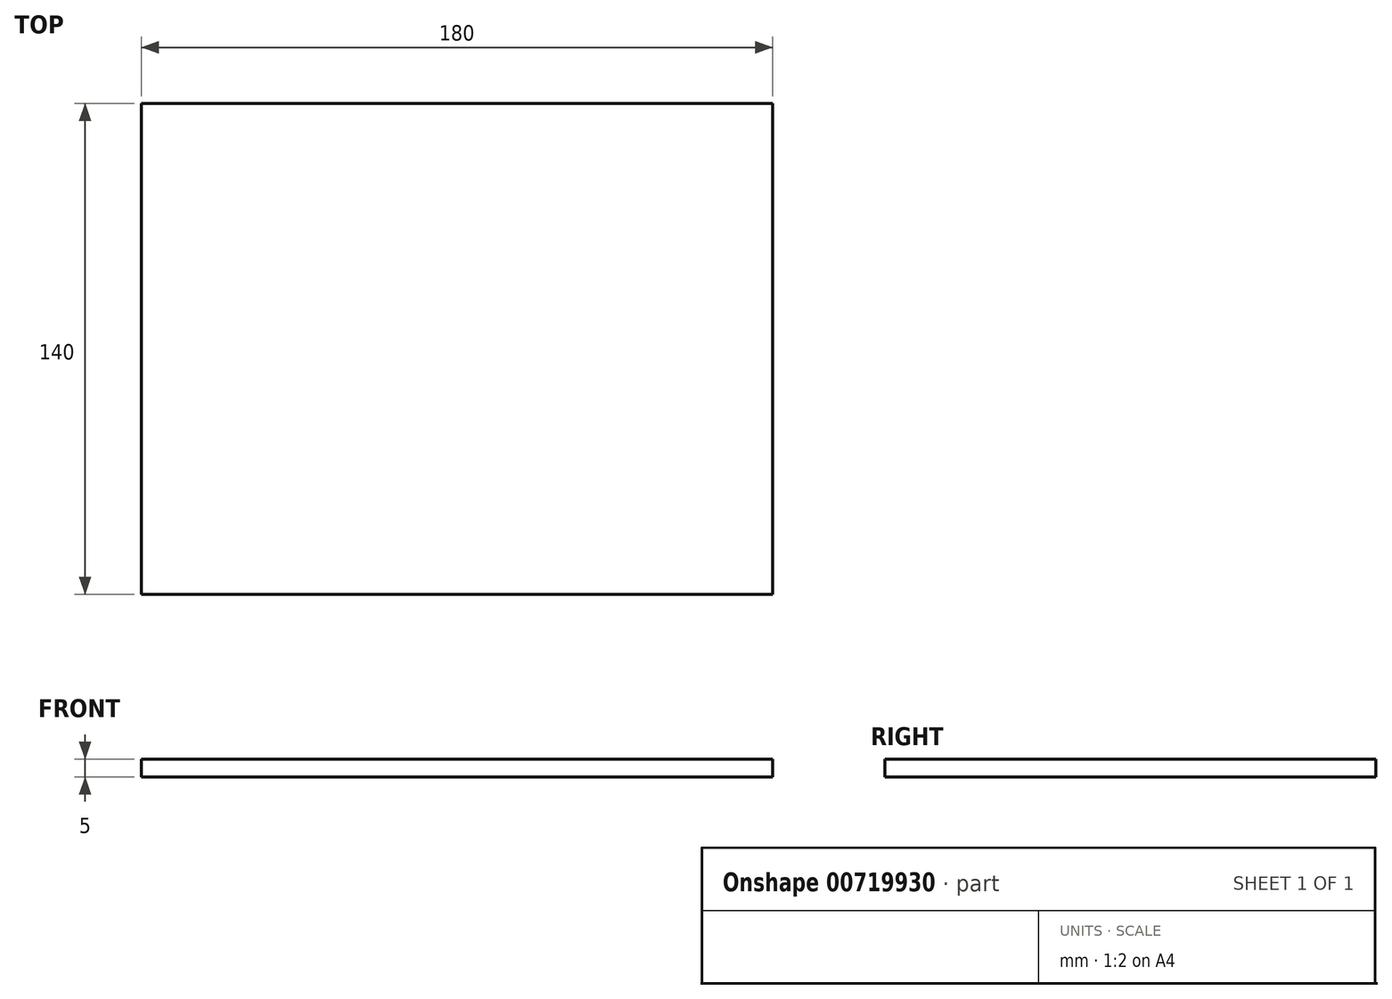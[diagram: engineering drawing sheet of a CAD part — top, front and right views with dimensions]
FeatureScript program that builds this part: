
annotation { "Feature Type Name" : "Feature", "Feature Type Description" : "" }
export const myFeature = defineFeature(function(context is Context, id is Id, definition is map)
    precondition{}
    {
        {
            var Q0;
            Q0=qCreatedBy(makeId("Top.planeOp"),FACE);
            var sketch = newSketch(context, id + "F0", { "sketchPlane" : qUnion([Q0])});
            skLineSegment(sketch, "E0.bottom", {"start": v(-180, 140) * mm, "end": v(0, 140) * mm});
            skLineSegment(sketch, "E0.top", {"start": v(-180, 0) * mm, "end": v(0, 0) * mm});
            skLineSegment(sketch, "E0.left", {"start": v(-180, 140) * mm, "end": v(-180, 0) * mm});
            skLineSegment(sketch, "E0.right", {"start": v(0, 140) * mm, "end": v(0, 0) * mm});
            skSolve(sketch);
        }
        {
            var Q0;
            Q0 = qSketchRegion(id + "F0", true);
            extrude(context, id + "F1", {"entities" : qUnion([Q0]), "depth" : 5 * mm, "offsetDistance" : 25 * mm});
        }
    });
